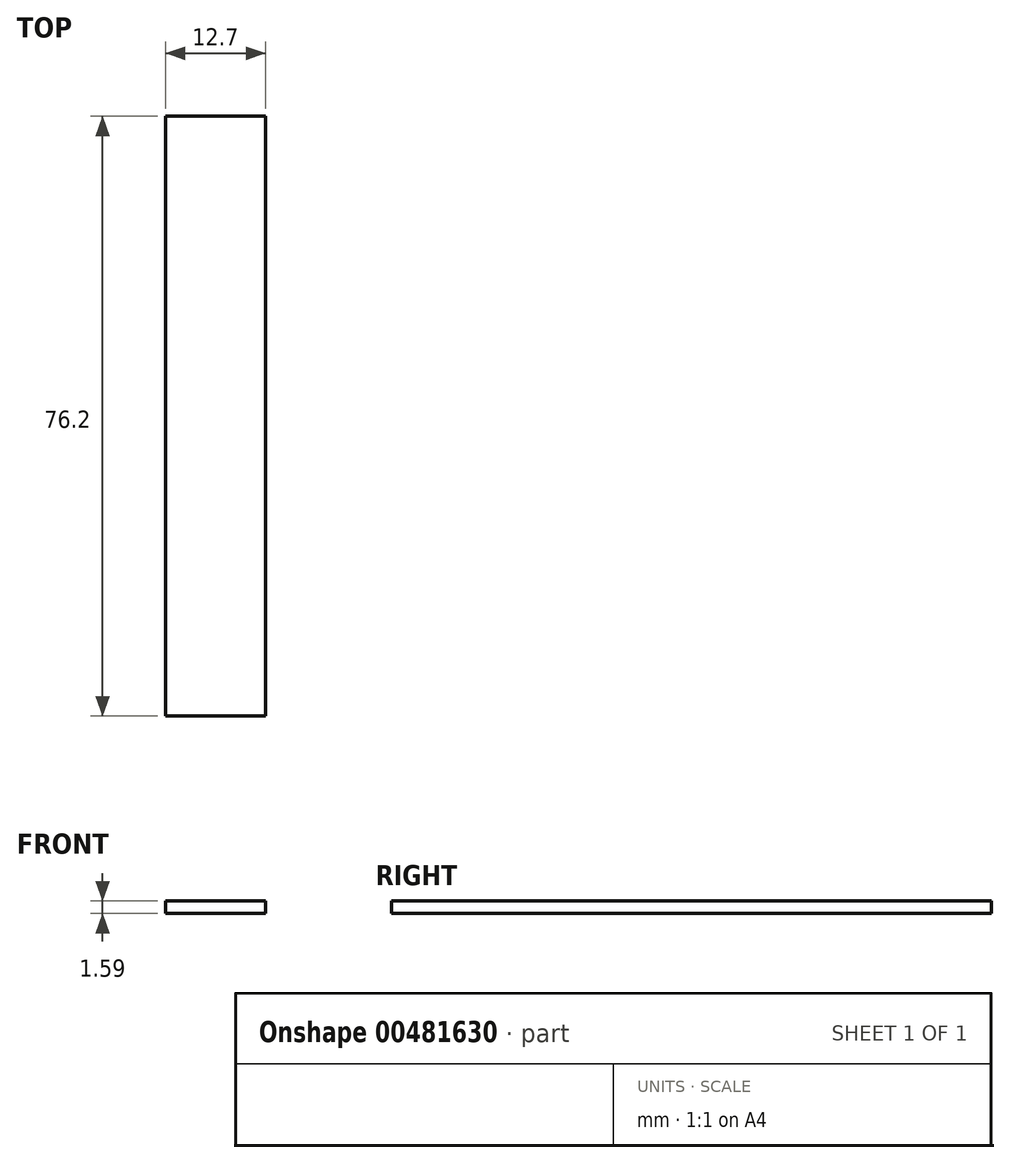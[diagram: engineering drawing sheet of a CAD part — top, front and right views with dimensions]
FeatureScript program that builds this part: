
annotation { "Feature Type Name" : "Feature", "Feature Type Description" : "" }
export const myFeature = defineFeature(function(context is Context, id is Id, definition is map)
    precondition{}
    {
        {
            var Q0;
            Q0=qCreatedBy(makeId("Front.planeOp"),FACE);
            var sketch = newSketch(context, id + "F0", { "sketchPlane" : qUnion([Q0])});
            skLineSegment(sketch, "E0.bottom", {"start": v(0, 0) * mm, "end": v(-12.7, 0) * mm});
            skLineSegment(sketch, "E0.top", {"start": v(0, 1.59) * mm, "end": v(-12.7, 1.59) * mm});
            skLineSegment(sketch, "E0.left", {"start": v(0, 0) * mm, "end": v(0, 1.59) * mm});
            skLineSegment(sketch, "E0.right", {"start": v(-12.7, 0) * mm, "end": v(-12.7, 1.59) * mm});
            skSolve(sketch);
        }
        {
            var Q0;
            Q0=makeQuery(id+"F0.imprint","IMPRINT",FACE,{"disambiguationData":[TD([[makeQuery(id+"F0.imprint","IMPRINT",EDGE,{"derivedFrom":sQuery(id+"F0.wireOp",EDGE,"E0.bottom")}),-1.0]])]});
            extrude(context, id + "F1", {"entities" : qUnion([Q0]), "depth" : 76.2 * mm});
        }
    });
